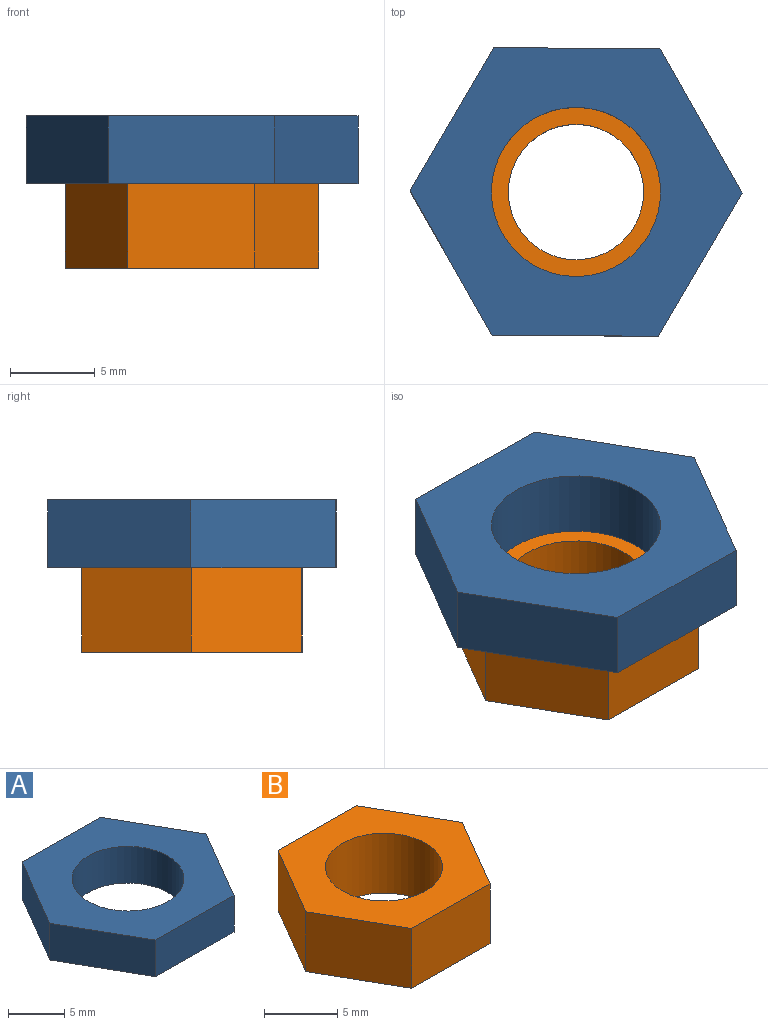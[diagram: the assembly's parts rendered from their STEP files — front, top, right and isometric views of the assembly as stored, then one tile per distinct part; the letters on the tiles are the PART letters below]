
ASSEMBLY  parts=2 mates=1
PART A: 9 faces, bbox 19.6x17.1x4 mm
  f0: plane 8.47x4.96mm, normal (0.86,-0.51,0), area 39.3mm2, adj f1,f6,f7,f8
  f1: plane 8.53x4.85mm, normal (0.87,0.49,0), area 39.3mm2, adj f0,f2,f7,f8
  f2: plane 9.81x4mm, normal (0.01,1,0), area 39.3mm2, adj f1,f3,f7,f8
  f3: plane 8.47x4.96mm, normal (-0.86,0.51,0), area 39.3mm2, adj f2,f4,f7,f8
  f4: plane 8.53x4.85mm, normal (-0.87,-0.49,0), area 39.3mm2, adj f3,f6,f7,f8
  f5: cylinder r=5mm len=10mm, axis (0,0,-1), area 125.7mm2, adj f7,f8
  f6: plane 9.81x4mm, normal (-0.01,-1,0), area 39.3mm2, adj f0,f4,f7,f8
  f7: plane 19.63x17.06mm, normal (0,0,1), area 171.7mm2, adj f0,f1,f2,f3,f4,f5,f6
  f8: plane 19.63x17.06mm, normal (0,0,-1), area 171.7mm2, adj f0,f1,f2,f3,f4,f5,f6
PART B: 9 faces, bbox 15x13x5 mm
  f0: plane 6.48x5mm, normal (0.86,-0.51,0), area 37.5mm2, adj f1,f6,f7,f8
  f1: plane 6.52x5mm, normal (0.87,0.49,0), area 37.5mm2, adj f0,f2,f7,f8
  f2: plane 7.51x5mm, normal (0.01,1,0), area 37.5mm2, adj f1,f3,f7,f8
  f3: plane 6.48x5mm, normal (-0.86,0.51,0), area 37.5mm2, adj f2,f4,f7,f8
  f4: plane 6.52x5mm, normal (-0.87,-0.49,0), area 37.5mm2, adj f3,f6,f7,f8
  f5: cylinder r=4mm len=8mm, axis (0,0,-1), area 125.7mm2, adj f7,f8
  f6: plane 7.51x5mm, normal (-0.01,-1,0), area 37.5mm2, adj f0,f4,f7,f8
  f7: plane 15.01x13.05mm, normal (0,0,1), area 96.1mm2, adj f0,f1,f2,f3,f4,f5,f6
  f8: plane 15.01x13.05mm, normal (0,0,-1), area 96.1mm2, adj f0,f1,f2,f3,f4,f5,f6
PLACE A t=(-5.57,-1.88,0)mm
PLACE B t=(-5.57,-1.88,-5)mm
MATE fastened B.f5 <-> A.f5  axis (0,0,1) through (-5.57,-1.88,0)mm
